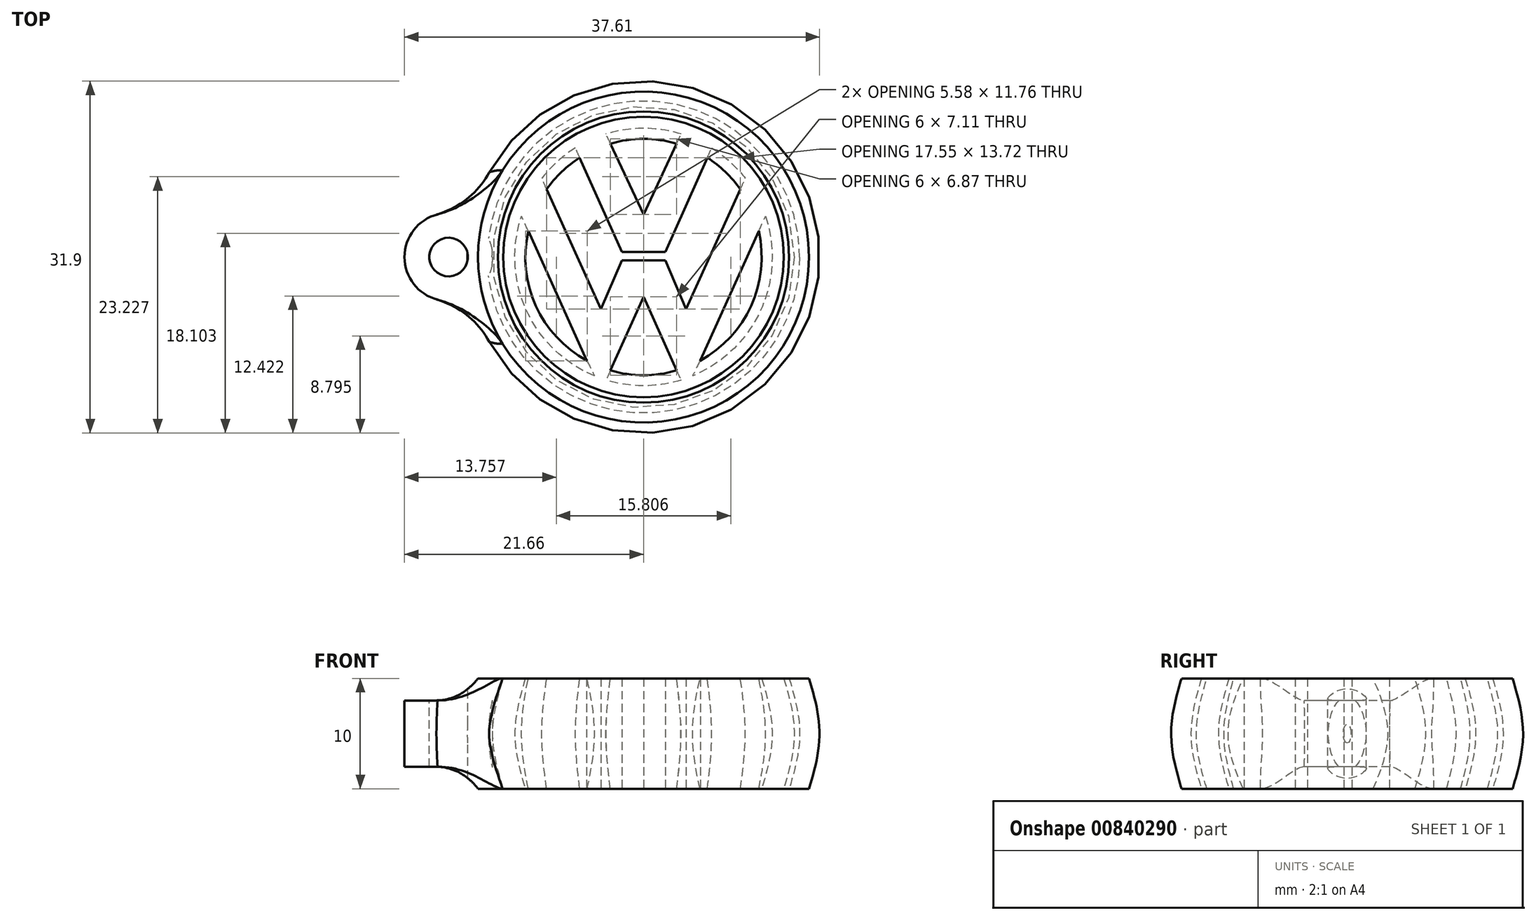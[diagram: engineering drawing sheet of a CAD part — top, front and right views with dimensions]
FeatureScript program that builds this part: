
annotation { "Feature Type Name" : "Feature", "Feature Type Description" : "" }
export const myFeature = defineFeature(function(context is Context, id is Id, definition is map)
    precondition{}
    {
        {
            var Q0;
            Q0=qCreatedBy(makeId("Right.planeOp"),FACE);
            var sketch = newSketch(context, id + "F0", { "sketchPlane" : qUnion([Q0])});
            skFitSpline(sketch, "E0", {"points": [v(-15, 5) * mm, v(-15.95, 0) * mm, v(-15, -5) * mm], "startDerivative": vector(-3, -10) * mm, "endDerivative": vector(3, -10) * mm});
            skLineSegment(sketch, "E1", {"start": v(-15, 5) * mm, "end": v(-13.2, 5) * mm});
            skLineSegment(sketch, "E2", {"start": v(-15, -5) * mm, "end": v(-13.2, -5) * mm});
            skFitSpline(sketch, "E3", {"points": [v(-13.2, 5) * mm, v(-14.15, 0) * mm, v(-13.2, -5) * mm], "startDerivative": vector(-3, -10) * mm, "endDerivative": vector(3, -10) * mm});
            skLineSegment(sketch, "E4", {"start": v(0, 5) * mm, "end": v(0, -5) * mm, "construction": true});
            skFitSpline(sketch, "E5", {"points": [v(-12.71, 5) * mm, v(-13.66, 0) * mm, v(-12.71, -5) * mm], "startDerivative": vector(-3, -10) * mm, "endDerivative": vector(3, -10) * mm});
            skLineSegment(sketch, "E6", {"start": v(-12.71, 5) * mm, "end": v(-10.71, 5) * mm});
            skLineSegment(sketch, "E7", {"start": v(-12.71, -5) * mm, "end": v(-10.71, -5) * mm});
            skFitSpline(sketch, "E8", {"points": [v(-10.71, 5) * mm, v(-11.66, 0) * mm, v(-10.71, -5) * mm], "startDerivative": vector(-3, -10) * mm, "endDerivative": vector(3, -10) * mm});
            skSolve(sketch);
        }
        {
            var Q0;
            Q0 = qSketchRegion(id + "F0", true);
            var Q1;
            Q1=sQuery(id+"F0.wireOp",EDGE,"E4");
            revolve(context, id + "F1", {"surfaceOperationType" : NewSurfaceOperationType.NEW, "entities" : qUnion([Q0]), "axis" : qUnion([Q1]), "revolveType" : RevolveType.FULL});
        }
        {
            var Q0;
            Q0=qCreatedBy(makeId("Top.planeOp"),FACE);
            var sketch = newSketch(context, id + "F2", { "sketchPlane" : qUnion([Q0])});
            skLineSegment(sketch, "E9", {"start": v(-1.97, 0.46) * mm, "end": v(0, 0.46) * mm});
            skLineSegment(sketch, "E10", {"start": v(0, 0.46) * mm, "end": v(0, 3.84) * mm});
            skLineSegment(sketch, "E11", {"start": v(0, -0.3) * mm, "end": v(-1.97, -0.3) * mm});
            skLineSegment(sketch, "E12", {"start": v(-1.97, -0.3) * mm, "end": v(-3.85, -4.7) * mm});
            skLineSegment(sketch, "E13", {"start": v(0, -3.6) * mm, "end": v(-3.8, -12.08) * mm});
            skLineSegment(sketch, "E14", {"start": v(0, 3.84) * mm, "end": v(-3.83, 12.07) * mm});
            skLineSegment(sketch, "E15", {"start": v(-1.97, 0.46) * mm, "end": v(-6.59, 10.81) * mm});
            skLineSegment(sketch, "E16", {"start": v(-3.85, -4.7) * mm, "end": v(-9.69, 8.15) * mm});
            skLineSegment(sketch, "E17", {"start": v(-5.15, -9.34) * mm, "end": v(-11.64, 4.98) * mm});
            skLineSegment(sketch, "E18", {"start": v(-5.15, -9.34) * mm, "end": v(-3.8, -12.08) * mm});
            skLineSegment(sketch, "E19", {"start": v(0, -3.6) * mm, "end": v(0, -0.3) * mm});
            skLineSegment(sketch, "E20.MirrorCS", {"start": v(1.97, -0.3) * mm, "end": v(3.85, -4.7) * mm});
            skLineSegment(sketch, "E21.MirrorCS", {"start": v(3.85, -4.7) * mm, "end": v(9.69, 8.15) * mm});
            skLineSegment(sketch, "E22.MirrorCS", {"start": v(0, 3.84) * mm, "end": v(3.83, 12.07) * mm});
            skLineSegment(sketch, "E23.MirrorCS", {"start": v(1.97, 0.46) * mm, "end": v(6.59, 10.81) * mm});
            skLineSegment(sketch, "E24.MirrorCS", {"start": v(5.15, -9.34) * mm, "end": v(11.64, 4.98) * mm});
            skLineSegment(sketch, "E25.MirrorCS", {"start": v(0, -3.6) * mm, "end": v(3.8, -12.08) * mm});
            skLineSegment(sketch, "E26.MirrorCS", {"start": v(5.15, -9.34) * mm, "end": v(3.8, -12.08) * mm});
            skLineSegment(sketch, "E27.MirrorCS", {"start": v(1.97, 0.46) * mm, "end": v(0, 0.46) * mm});
            skLineSegment(sketch, "E28.MirrorCS", {"start": v(0, -0.3) * mm, "end": v(1.97, -0.3) * mm});
            skFitSpline(sketch, "E29", {"points": [v(-9.69, 8.15) * mm, v(-10.77, 6.65) * mm, v(-11.64, 4.98) * mm], "startDerivative": vector(-2.27, -2.95) * mm, "endDerivative": vector(-1.64, -3.39) * mm});
            skFitSpline(sketch, "E30", {"points": [v(6.59, 10.81) * mm, v(5.25, 11.52) * mm, v(3.83, 12.07) * mm], "startDerivative": vector(-2.65, 1.49) * mm, "endDerivative": vector(-2.86, 1.02) * mm});
            skFitSpline(sketch, "E31", {"points": [v(-3.83, 12.07) * mm, v(-5.2, 11.55) * mm, v(-6.59, 10.81) * mm], "startDerivative": vector(-2.78, -0.99) * mm, "endDerivative": vector(-2.73, -1.52) * mm});
            skFitSpline(sketch, "E32", {"points": [v(9.69, 8.15) * mm, v(10.85, 6.52) * mm, v(11.64, 4.98) * mm], "startDerivative": vector(2.4, -3.15) * mm, "endDerivative": vector(1.5, -3.2) * mm});
            skSolve(sketch);
        }
        {
            var Q0;
            Q0=makeQuery(id+"F1.opRevolve","SWEPT_FACE",FACE,{"disambiguationData":[OSD([sQuery(id+"F0.wireOp",EDGE,"E1")])]});
            var sketch = newSketch(context, id + "F3", { "sketchPlane" : qUnion([Q0])});
            skCircle(sketch, "E33", {"center": v(-17.66, 0) * mm, "radius": 4 * mm});
            skCircle(sketch, "E34", {"center": v(-17.66, 0) * mm, "radius": 1.75 * mm});
            skSolve(sketch);
        }
        {
            var Q0;
            Q0 = qSketchRegion(id + "F3", true);
            var Q1;
            Q1=makeQuery(id+"F1.opRevolve","SWEPT_BODY",BODY,{"disambiguationData":[OSD([sQuery(id+"F0.wireOp",EDGE,"E0"),sQuery(id+"F0.wireOp",EDGE,"E1"),sQuery(id+"F0.wireOp",EDGE,"E2"),sQuery(id+"F0.wireOp",EDGE,"E3")])]});
            extrude(context, id + "F4", {"entities" : qUnion([Q0]), "operationType" : NewBodyOperationType.ADD, "oppositeDirection" : true, "depth" : 8 * mm, "endBoundEntityBody" : qUnion([Q1]), "hasOffset" : true, "offsetDistance" : 25 * mm, "hasSecondDirection" : true, "secondDirectionOppositeDirection" : true, "secondDirectionDepth" : 2 * mm});
        }
        {
            var Q0;
            Q0=makeQuery(id+"F4.boolean.opBoolean","INTERSECT",EDGE,{"disambiguationData":[OD(0.0)],"derivedFrom":[makeQuery(id+"F1.opRevolve","SWEPT_FACE",FACE,{"disambiguationData":[OSD([sQuery(id+"F0.wireOp",EDGE,"E0")])]}),makeQuery(id+"F4.opExtrude","SWEPT_FACE",FACE,{"disambiguationData":[OSD([sQuery(id+"F3.wireOp",EDGE,"E33")])]})]});
            var Q1;
            Q1=makeQuery(id+"F4.boolean.opBoolean","INTERSECT",EDGE,{"disambiguationData":[OD(1.0)],"derivedFrom":[makeQuery(id+"F1.opRevolve","SWEPT_FACE",FACE,{"disambiguationData":[OSD([sQuery(id+"F0.wireOp",EDGE,"E0")])]}),makeQuery(id+"F4.opExtrude","SWEPT_FACE",FACE,{"disambiguationData":[OSD([sQuery(id+"F3.wireOp",EDGE,"E33")])]})]});
            fillet(context, id + "F5", {"entities" : qUnion([Q0, Q1]), "radius" : 8 * mm, "tangentPropagation" : true, "allowEdgeOverflow" : false});
        }
        {
            var Q0;
            Q0=makeQuery(id+"F4.boolean.opBoolean","INTERSECT",EDGE,{"derivedFrom":[makeQuery(id+"F1.opRevolve","SWEPT_FACE",FACE,{"disambiguationData":[OSD([sQuery(id+"F0.wireOp",EDGE,"E0")])]}),makeQuery(id+"F4.opExtrude","CAP_FACE",FACE,{"disambiguationData":[OSD([sQuery(id+"F3.wireOp",EDGE,"E33"),sQuery(id+"F3.wireOp",EDGE,"E34")])],"isStart":false})]});
            var Q1;
            Q1=makeQuery(id+"F4.boolean.opBoolean","INTERSECT",EDGE,{"derivedFrom":[makeQuery(id+"F1.opRevolve","SWEPT_FACE",FACE,{"disambiguationData":[OSD([sQuery(id+"F0.wireOp",EDGE,"E0")])]}),makeQuery(id+"F4.opExtrude","CAP_FACE",FACE,{"disambiguationData":[OSD([sQuery(id+"F3.wireOp",EDGE,"E33"),sQuery(id+"F3.wireOp",EDGE,"E34")])],"isStart":true})]});
            fillet(context, id + "F6", {"entities" : qUnion([Q0, Q1]), "radius" : 5 * mm, "tangentPropagation" : true, "allowEdgeOverflow" : false});
        }
        {
            var Q0;
            Q0=makeQuery(id+"F2.imprint","IMPRINT",FACE,{"disambiguationData":[TD([[makeQuery(id+"F2.imprint","IMPRINT",EDGE,{"derivedFrom":sQuery(id+"F2.wireOp",EDGE,"E11")}),1.0]])]});
            var Q1;
            Q1=makeQuery(id+"F2.imprint","IMPRINT",FACE,{"disambiguationData":[TD([[makeQuery(id+"F2.imprint","IMPRINT",EDGE,{"derivedFrom":sQuery(id+"F2.wireOp",EDGE,"E19")}),-1.0]])]});
            var Q2;
            Q2=makeQuery(id+"F2.imprint","IMPRINT",FACE,{"disambiguationData":[TD([[makeQuery(id+"F2.imprint","IMPRINT",EDGE,{"derivedFrom":sQuery(id+"F2.wireOp",EDGE,"E10")}),-1.0]])]});
            var Q3;
            Q3=makeQuery(id+"F2.imprint","IMPRINT",FACE,{"disambiguationData":[TD([[makeQuery(id+"F2.imprint","IMPRINT",EDGE,{"derivedFrom":sQuery(id+"F2.wireOp",EDGE,"E9")}),1.0]])]});
            var Q4;
            Q4=makeQuery(id+"F1.opRevolve","SWEPT_FACE",FACE,{"disambiguationData":[OSD([sQuery(id+"F0.wireOp",EDGE,"E6")])]});
            var Q5;
            Q5=makeQuery(id+"F1.opRevolve","SWEPT_FACE",FACE,{"disambiguationData":[OSD([sQuery(id+"F0.wireOp",EDGE,"E7")])]});
            extrude(context, id + "F7", {"entities" : qUnion([Q0, Q1, Q2, Q3]), "operationType" : NewBodyOperationType.ADD, "endBound" : BoundingType.UP_TO_SURFACE, "depth" : 25 * mm, "endBoundEntityFace" : qUnion([Q4]), "offsetDistance" : 25 * mm, "hasSecondDirection" : true, "secondDirectionBound" : SecondDirectionBoundingType.UP_TO_SURFACE, "secondDirectionOppositeDirection" : true, "secondDirectionDepth" : 25 * mm, "secondDirectionBoundEntityFace" : qUnion([Q5])});
        }
    });
